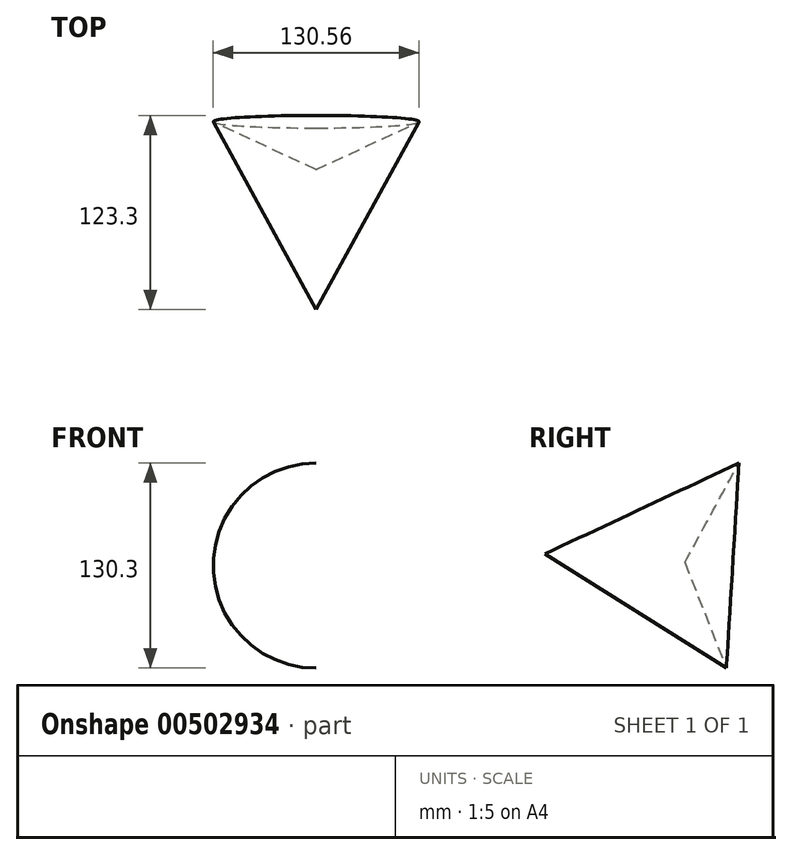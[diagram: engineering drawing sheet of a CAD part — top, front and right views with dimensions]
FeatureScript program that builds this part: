
annotation { "Feature Type Name" : "Feature", "Feature Type Description" : "" }
export const myFeature = defineFeature(function(context is Context, id is Id, definition is map)
    precondition{}
    {
        {
            var Q0;
            Q0=qCreatedBy(makeId("Right.planeOp"),FACE);
            var sketch = newSketch(context, id + "F0", { "sketchPlane" : qUnion([Q0])});
            skLineSegment(sketch, "E0", {"start": v(0, 0) * mm, "end": v(-60.15, -28.2) * mm});
            skLineSegment(sketch, "E1", {"start": v(-60.15, -28.2) * mm, "end": v(28.78, -33.67) * mm});
            skLineSegment(sketch, "E2", {"start": v(28.78, -33.67) * mm, "end": v(63.15, 29.61) * mm});
            skLineSegment(sketch, "E3", {"start": v(63.15, 29.61) * mm, "end": v(0, 0) * mm});
            skSolve(sketch);
        }
        {
            var Q0;
            Q0 = qSketchRegion(id + "F0", true);
            var Q1;
            Q1=sQuery(id+"F0.wireOp",EDGE,"E1");
            revolve(context, id + "F1", {"entities" : qUnion([Q0]), "axis" : qUnion([Q1]), "revolveType" : RevolveType.FULL});
        }
    });
